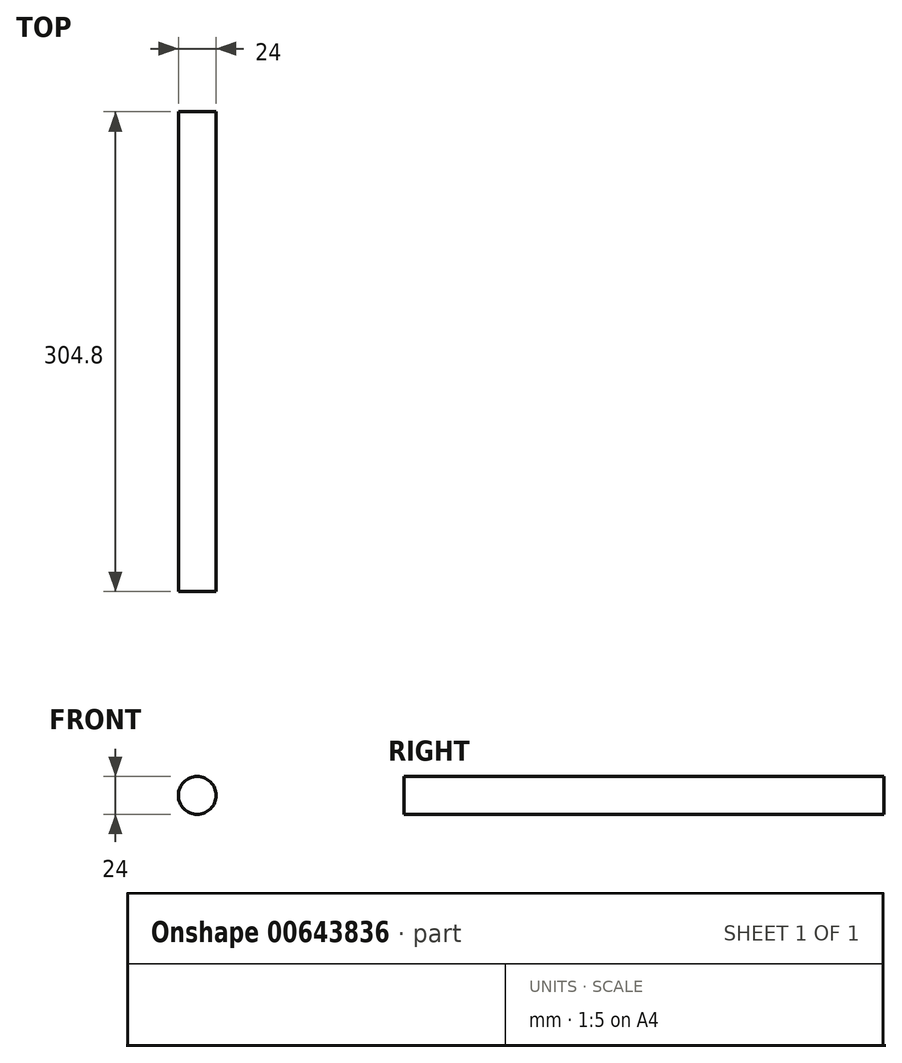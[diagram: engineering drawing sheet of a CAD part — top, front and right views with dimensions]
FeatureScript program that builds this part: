
annotation { "Feature Type Name" : "Feature", "Feature Type Description" : "" }
export const myFeature = defineFeature(function(context is Context, id is Id, definition is map)
    precondition{}
    {
        {
            var Q0;
            Q0=qCreatedBy(makeId("Front.planeOp"),FACE);
            var sketch = newSketch(context, id + "F0", { "sketchPlane" : qUnion([Q0])});
            skCircle(sketch, "E0", {"center": v(0, 0) * mm, "radius": 12 * mm});
            skSolve(sketch);
        }
        {
            var Q0;
            Q0=makeQuery(id+"F0.imprint","IMPRINT",FACE,{"disambiguationData":[TD([[makeQuery(id+"F0.imprint","IMPRINT",EDGE,{"derivedFrom":sQuery(id+"F0.wireOp",EDGE,"E0")}),1.0]])]});
            extrude(context, id + "F1", {"entities" : qUnion([Q0]), "depth" : 304.8 * mm, "offsetDistance" : 25.4 * mm});
        }
    });
